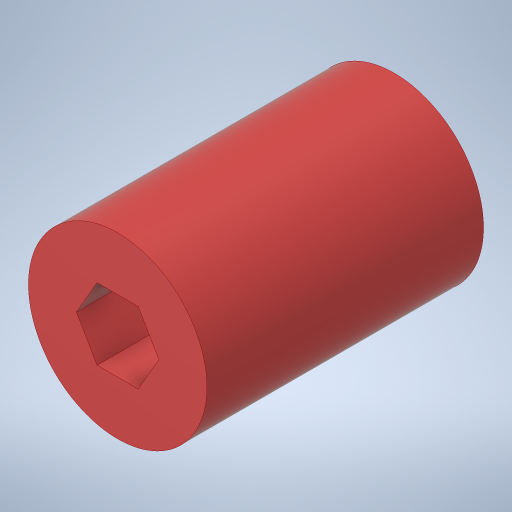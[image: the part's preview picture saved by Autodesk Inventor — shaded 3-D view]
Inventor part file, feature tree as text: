
AUTODESK INVENTOR PART (.ipt)
format: ipt  version: 2023 (Build 270158000, 158)  size: 222,208 bytes
history: native  units: in
note: dims shown in document units (in); Inventor stores cm internally (conversion verified against a paired STEP export)
features: extrude x1, sketch x1
ambient origin geometry x8: Origin, YZ Plane, XZ Plane, XY Plane, X Axis, Y Axis, Z Axis, Center Point
bodies: Solid1 (feature_tree)
feature tree (2):
  extrude  "Extrusion1"  Depth=0.5in
  sketch  "Sketch1"  dims[d0=1.25in d1=0.5in d2=1.9375in d3=0.0in]
